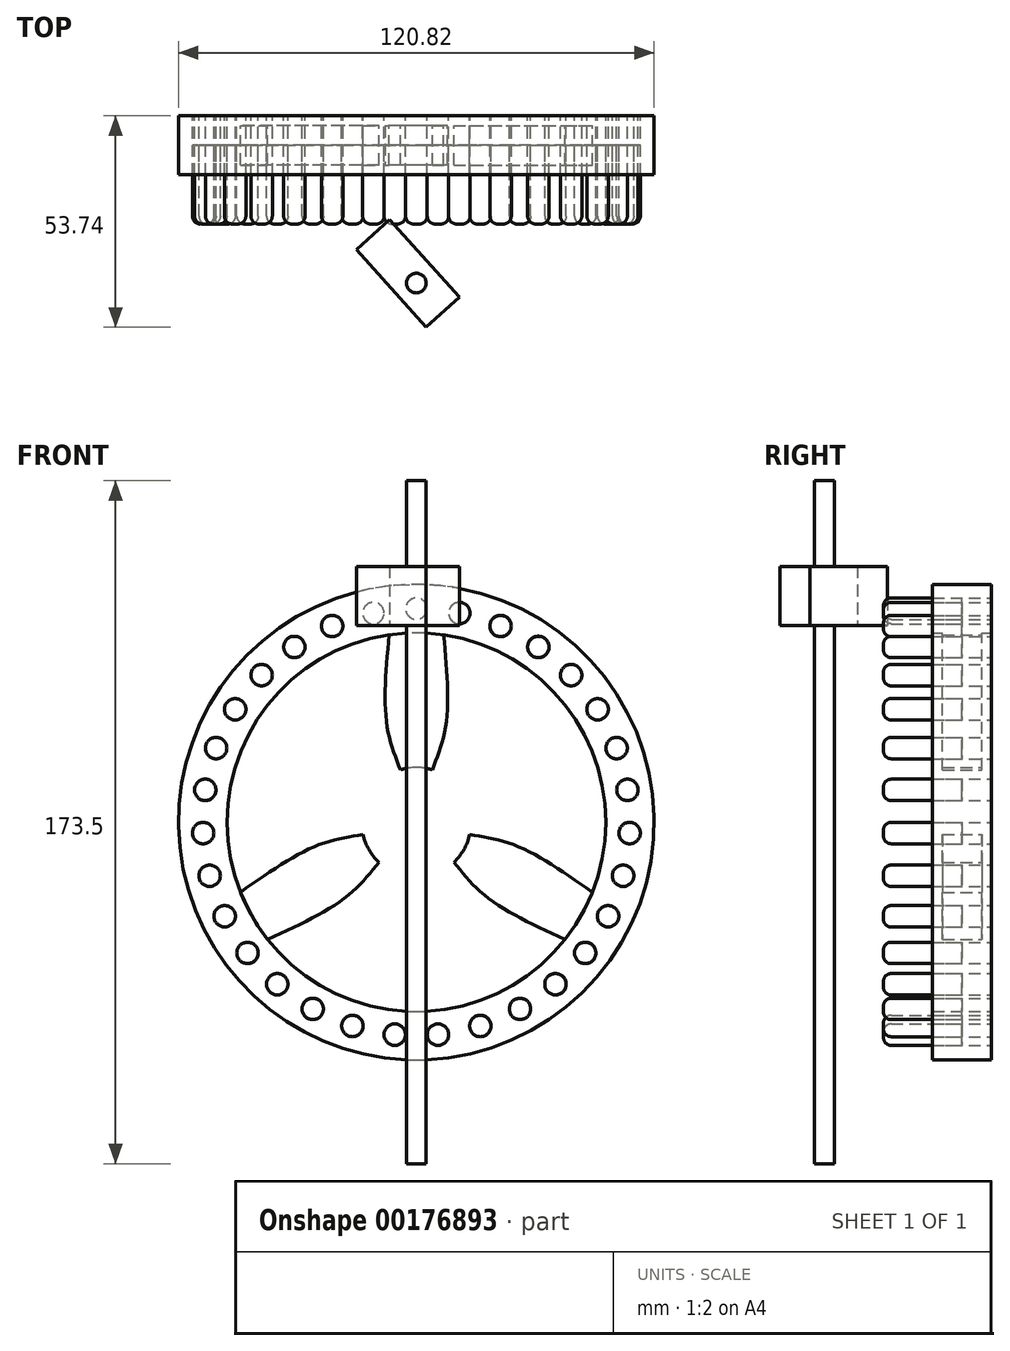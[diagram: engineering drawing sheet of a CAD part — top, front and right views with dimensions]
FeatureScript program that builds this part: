
annotation { "Feature Type Name" : "Feature", "Feature Type Description" : "" }
export const myFeature = defineFeature(function(context is Context, id is Id, definition is map)
    precondition{}
    {
        {
            var Q0;
            Q0=qCreatedBy(makeId("Front.planeOp"),FACE);
            var sketch = newSketch(context, id + "F0", { "sketchPlane" : qUnion([Q0])});
            skCircle(sketch, "E0", {"center": v(0, 0) * mm, "radius": 13.92 * mm});
            skCircle(sketch, "E1", {"center": v(0, 0) * mm, "radius": 48.1 * mm});
            skCircle(sketch, "E2", {"center": v(0, 0) * mm, "radius": 60.4 * mm});
            skFitSpline(sketch, "E3", {"points": [v(-4.04, 13.32) * mm, v(-7.58, 25.47) * mm, v(-6.93, 47.6) * mm], "startDerivative": vector(-10.25, 25.95) * mm, "endDerivative": vector(3.83, 41.84) * mm});
            skFitSpline(sketch, "E4.MirrorCS", {"points": [v(4.04, 13.32) * mm, v(7.58, 25.47) * mm, v(6.93, 47.6) * mm], "startDerivative": vector(10.25, 25.95) * mm, "endDerivative": vector(-3.83, 41.84) * mm});
            skCircle(sketch, "E5", {"center": v(0, 54.25) * mm, "radius": 2.72 * mm});
            skCircle(sketch, "E6.1.0", {"center": v(-10.92, 53.14) * mm, "radius": 2.72 * mm});
            skCircle(sketch, "E6.2.0", {"center": v(-21.4, 49.85) * mm, "radius": 2.72 * mm});
            skLineSegment(sketch, "E6.anchor1", {"start": v(0, 0) * mm, "end": v(0, 54.25) * mm, "construction": true});
            skLineSegment(sketch, "E6.anchor2", {"start": v(0, 0) * mm, "end": v(10.92, 53.14) * mm, "construction": true});
            skCircle(sketch, "E7.1.3.0", {"center": v(-31, 44.53) * mm, "radius": 2.72 * mm});
            skCircle(sketch, "E7.1.4.0", {"center": v(-39.32, 37.38) * mm, "radius": 2.72 * mm});
            skCircle(sketch, "E7.1.5.0", {"center": v(-46.04, 28.7) * mm, "radius": 2.72 * mm});
            skCircle(sketch, "E7.1.6.0", {"center": v(-50.87, 18.84) * mm, "radius": 2.72 * mm});
            skCircle(sketch, "E7.1.7.0", {"center": v(-53.62, 8.21) * mm, "radius": 2.72 * mm});
            skCircle(sketch, "E7.1.8.0", {"center": v(-54.18, -2.75) * mm, "radius": 2.72 * mm});
            skCircle(sketch, "E7.1.9.0", {"center": v(-52.52, -13.6) * mm, "radius": 2.72 * mm});
            skCircle(sketch, "E7.1.10.0", {"center": v(-48.7, -23.9) * mm, "radius": 2.72 * mm});
            skCircle(sketch, "E7.1.11.0", {"center": v(-42.9, -33.2) * mm, "radius": 2.72 * mm});
            skCircle(sketch, "E7.1.12.0", {"center": v(-35.34, -41.16) * mm, "radius": 2.72 * mm});
            skCircle(sketch, "E7.1.13.0", {"center": v(-26.33, -47.43) * mm, "radius": 2.72 * mm});
            skCircle(sketch, "E7.1.14.0", {"center": v(-16.24, -51.76) * mm, "radius": 2.72 * mm});
            skCircle(sketch, "E7.1.15.0", {"center": v(-5.49, -53.97) * mm, "radius": 2.72 * mm});
            skCircle(sketch, "E7.1.16.0", {"center": v(5.49, -53.97) * mm, "radius": 2.72 * mm});
            skCircle(sketch, "E7.1.17.0", {"center": v(16.24, -51.76) * mm, "radius": 2.72 * mm});
            skCircle(sketch, "E7.1.18.0", {"center": v(26.33, -47.43) * mm, "radius": 2.72 * mm});
            skCircle(sketch, "E7.1.19.0", {"center": v(35.34, -41.16) * mm, "radius": 2.72 * mm});
            skCircle(sketch, "E7.1.20.0", {"center": v(42.9, -33.2) * mm, "radius": 2.72 * mm});
            skCircle(sketch, "E7.1.21.0", {"center": v(48.7, -23.9) * mm, "radius": 2.72 * mm});
            skCircle(sketch, "E7.1.22.0", {"center": v(52.52, -13.6) * mm, "radius": 2.72 * mm});
            skCircle(sketch, "E7.1.23.0", {"center": v(54.18, -2.75) * mm, "radius": 2.72 * mm});
            skCircle(sketch, "E7.1.24.0", {"center": v(53.62, 8.21) * mm, "radius": 2.72 * mm});
            skCircle(sketch, "E7.1.25.0", {"center": v(50.87, 18.84) * mm, "radius": 2.72 * mm});
            skCircle(sketch, "E7.1.26.0", {"center": v(46.04, 28.7) * mm, "radius": 2.72 * mm});
            skCircle(sketch, "E7.1.27.0", {"center": v(39.32, 37.38) * mm, "radius": 2.72 * mm});
            skCircle(sketch, "E7.1.28.0", {"center": v(31, 44.53) * mm, "radius": 2.72 * mm});
            skCircle(sketch, "E7.1.29.0", {"center": v(21.4, 49.85) * mm, "radius": 2.72 * mm});
            skCircle(sketch, "E7.1.30.0", {"center": v(10.92, 53.14) * mm, "radius": 2.72 * mm});
            skCircle(sketch, "E8", {"center": v(0, 0) * mm, "radius": 5.4 * mm});
            skSolve(sketch);
        }
        {
            var Q0;
            {var subQ0=sQuery(id+"F0.wireOp",EDGE,"E3");Q0=makeQuery(id+"F0.imprint","IMPRINT",FACE,{"disambiguationData":[TD([[makeQuery(id+"F0.imprint","IMPRINT",EDGE,{"derivedFrom":subQ0}),-1.0]])]});}
            var Q1;
            Q1=sQuery(id+"F0.wireOp",EDGE,"E3");
            var Q2;
            Q2=sQuery(id+"F0.wireOp",EDGE,"E4.MirrorCS");
            extrude(context, id + "F1", {"entities" : qUnion([Q0]), "surfaceEntities" : qUnion([Q1, Q2]), "endBound" : BoundingType.SYMMETRIC, "depth" : 10 * mm});
        }
        {
            var Q0;
            Q0=qCreatedBy(makeId("Right.planeOp"),FACE);
            var sketch = newSketch(context, id + "F2", { "sketchPlane" : qUnion([Q0])});
            skLineSegment(sketch, "E9", {"start": v(-49.2, 0) * mm, "end": v(48.61, 0) * mm});
            skSolve(sketch);
        }
        {
            var Q0;
            Q0=makeQuery(id+"F1.opExtrude","SWEPT_BODY",BODY,{"disambiguationData":[OSD([sQuery(id+"F0.wireOp",EDGE,"E1"),sQuery(id+"F0.wireOp",EDGE,"E3"),sQuery(id+"F0.wireOp",EDGE,"E4.MirrorCS"),sQuery(id+"F0.wireOp",EDGE,"E0")])]});
            var Q1;
            Q1=sQuery(id+"F2.wireOp",EDGE,"E9");
            circularPattern(context, id + "F3", {"entities" : qUnion([Q0]), "axis" : qUnion([Q1]), "angle" : 120 * degree, "instanceCount" : 3});
        }
        {
            var Q0;
            Q0=makeQuery(id+"F0.imprint","IMPRINT",FACE,{"disambiguationData":[TD([[makeQuery(id+"F0.imprint","IMPRINT",EDGE,{"derivedFrom":sQuery(id+"F0.wireOp",EDGE,"E2")}),1.0]])]});
            var Q1;
            {var subQ0=sQuery(id+"F0.wireOp",EDGE,"E0");var subQ1=makeQuery(id+"F0.imprint","INTERSECT",VERTEX,{"derivedFrom":[sQuery(id+"F0.wireOp",EDGE,"E3"),subQ0]});Q1=makeQuery(id+"F0.imprint","IMPRINT",FACE,{"disambiguationData":[TD([[makeQuery(id+"F0.imprint","IMPRINT",EDGE,{"disambiguationData":[TD([[subQ1,1.0]])],"derivedFrom":subQ0}),1.0]])]});}
            extrude(context, id + "F4", {"entities" : qUnion([Q0, Q1]), "operationType" : NewBodyOperationType.ADD, "endBound" : BoundingType.SYMMETRIC, "depth" : 15 * mm});
        }
        {
            var Q0;
            Q0=makeQuery(id+"F0.imprint","IMPRINT",FACE,{"disambiguationData":[TD([[makeQuery(id+"F0.imprint","IMPRINT",EDGE,{"derivedFrom":sQuery(id+"F0.wireOp",EDGE,"E5")}),1.0]])]});
            extrude(context, id + "F5", {"entities" : qUnion([Q0]), "depth" : 20 * mm});
        }
        {
            var Q0;
            Q0=makeQuery(id+"F5.opExtrude","CAP_EDGE",EDGE,{"disambiguationData":[OSD([sQuery(id+"F0.wireOp",EDGE,"E5")])],"isStart":false});
            fillet(context, id + "F6", {"entities" : qUnion([Q0]), "radius" : 2 * mm, "tangentPropagation" : true, "allowEdgeOverflow" : false});
        }
        {
            var Q0;
            Q0=makeQuery(id+"F5.opExtrude","SWEPT_BODY",BODY,{"disambiguationData":[OSD([sQuery(id+"F0.wireOp",EDGE,"E5")])]});
            var Q1;
            Q1=sQuery(id+"F2.wireOp",EDGE,"E9");
            circularPattern(context, id + "F7", {"entities" : qUnion([Q0]), "axis" : qUnion([Q1]), "angle" : 11.6 * degree, "instanceCount" : 31});
        }
        {
            var Q0;
            Q0=qCreatedBy(makeId("Right.planeOp"),FACE);
            var sketch = newSketch(context, id + "F8", { "sketchPlane" : qUnion([Q0])});
            skLineSegment(sketch, "E10", {"start": v(-35, 94.75) * mm, "end": v(-35, -91.5) * mm});
            skLineSegment(sketch, "E11.bottom", {"start": v(-32.5, 86.75) * mm, "end": v(-37.5, 86.75) * mm});
            skLineSegment(sketch, "E11.top", {"start": v(-32.5, -86.75) * mm, "end": v(-37.5, -86.75) * mm});
            skLineSegment(sketch, "E11.left", {"start": v(-32.5, 86.75) * mm, "end": v(-32.5, -86.75) * mm});
            skLineSegment(sketch, "E11.right", {"start": v(-37.5, 86.75) * mm, "end": v(-37.5, -86.75) * mm});
            skPoint(sketch, "E11.middle", {"position": v(-35, 0) * mm});
            skSolve(sketch);
        }
        {
            var Q0;
            {var subQ5=sQuery(id+"F8.wireOp",EDGE,"E11.right");Q0=makeQuery(id+"F8.imprint","IMPRINT",FACE,{"disambiguationData":[TD([[makeQuery(id+"F8.imprint","IMPRINT",EDGE,{"derivedFrom":subQ5}),1.0]])]});}
            var Q1;
            Q1=sQuery(id+"F8.wireOp",EDGE,"E10");
            revolve(context, id + "F9", {"entities" : qUnion([Q0]), "axis" : qUnion([Q1]), "revolveType" : RevolveType.FULL});
        }
        {
            var Q0;
            Q0=qCreatedBy(makeId("Top.planeOp"),FACE);
            cPlane(context, id + "F10", {"entities" : qUnion([Q0]), "cplaneType" : CPlaneType.OFFSET, "offset" : 50 * mm, "width" : 150 * mm, "height" : 150 * mm});
        }
        {
            var Q0;
            Q0=qCreatedBy(id+"F10.planeOp",FACE);
            var sketch = newSketch(context, id + "F11", { "sketchPlane" : qUnion([Q0])});
            skLineSegment(sketch, "E12", {"start": v(2.44, -46.24) * mm, "end": v(-15.25, -26.56) * mm});
            skLineSegment(sketch, "E13", {"start": v(-15.25, -26.56) * mm, "end": v(-6.78, -18.94) * mm});
            skLineSegment(sketch, "E14", {"start": v(-6.78, -18.94) * mm, "end": v(10.92, -38.62) * mm});
            skLineSegment(sketch, "E15", {"start": v(10.92, -38.62) * mm, "end": v(2.44, -46.24) * mm});
            skCircle(sketch, "E16.0", {"center": v(0, -35) * mm, "radius": 2.5 * mm});
            skLineSegment(sketch, "E17", {"start": v(0, -35) * mm, "end": v(4.24, -31.19) * mm});
            skLineSegment(sketch, "E18", {"start": v(0, -35) * mm, "end": v(-4.24, -38.81) * mm});
            skSolve(sketch);
        }
        {
            var Q0;
            {var subQ6=sQuery(id+"F11.wireOp",EDGE,"E13");Q0=makeQuery(id+"F11.imprint","IMPRINT",FACE,{"disambiguationData":[TD([[makeQuery(id+"F11.imprint","IMPRINT",EDGE,{"derivedFrom":subQ6}),-1.0]])]});}
            var Q1;
            {var subQ5=sQuery(id+"F11.wireOp",EDGE,"E15");Q1=makeQuery(id+"F11.imprint","IMPRINT",FACE,{"disambiguationData":[TD([[makeQuery(id+"F11.imprint","IMPRINT",EDGE,{"derivedFrom":subQ5}),-1.0]])]});}
            extrude(context, id + "F12", {"entities" : qUnion([Q0, Q1]), "operationType" : NewBodyOperationType.ADD, "depth" : 15 * mm});
        }
    });
